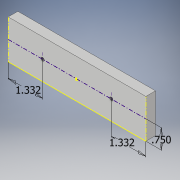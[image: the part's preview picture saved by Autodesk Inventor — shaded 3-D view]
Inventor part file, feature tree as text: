
AUTODESK INVENTOR PART (.ipt)
format: ipt  version: 2017 (Build 210142000, 142)  size: 104,960 bytes
history: native  units: in
note: dims shown in document units (in); Inventor stores cm internally (conversion verified against a paired STEP export)
features: sketch x2, extrude x1, hole x1
ambient origin geometry x8: Origin, YZ Plane, XZ Plane, XY Plane, X Axis, Y Axis, Z Axis, Center Point
bodies: Solid1 (feature_tree)
feature tree (4):
  extrude  "Extrusion1"  Depth=1.5in
  hole  "Hole1"  [1 undecoded]
  sketch  "Sketch1"  dims[d0=5.326in d1=1.5in]
  sketch  "Sketch2"  dims[d2=0.375in d3=0.0in d4=1.332in d5=1.332in d6=0.128in d7=0.315in d8=0.375in d9=0.25in d10=0.5635in d11=0.465in d12=0.8108in d13=0.75in]
note: 1 required parameter value undecoded (feature->parameter linkage not recoverable at this tier; creation-order binding heuristic only, values carry confidence <= 0.55)
